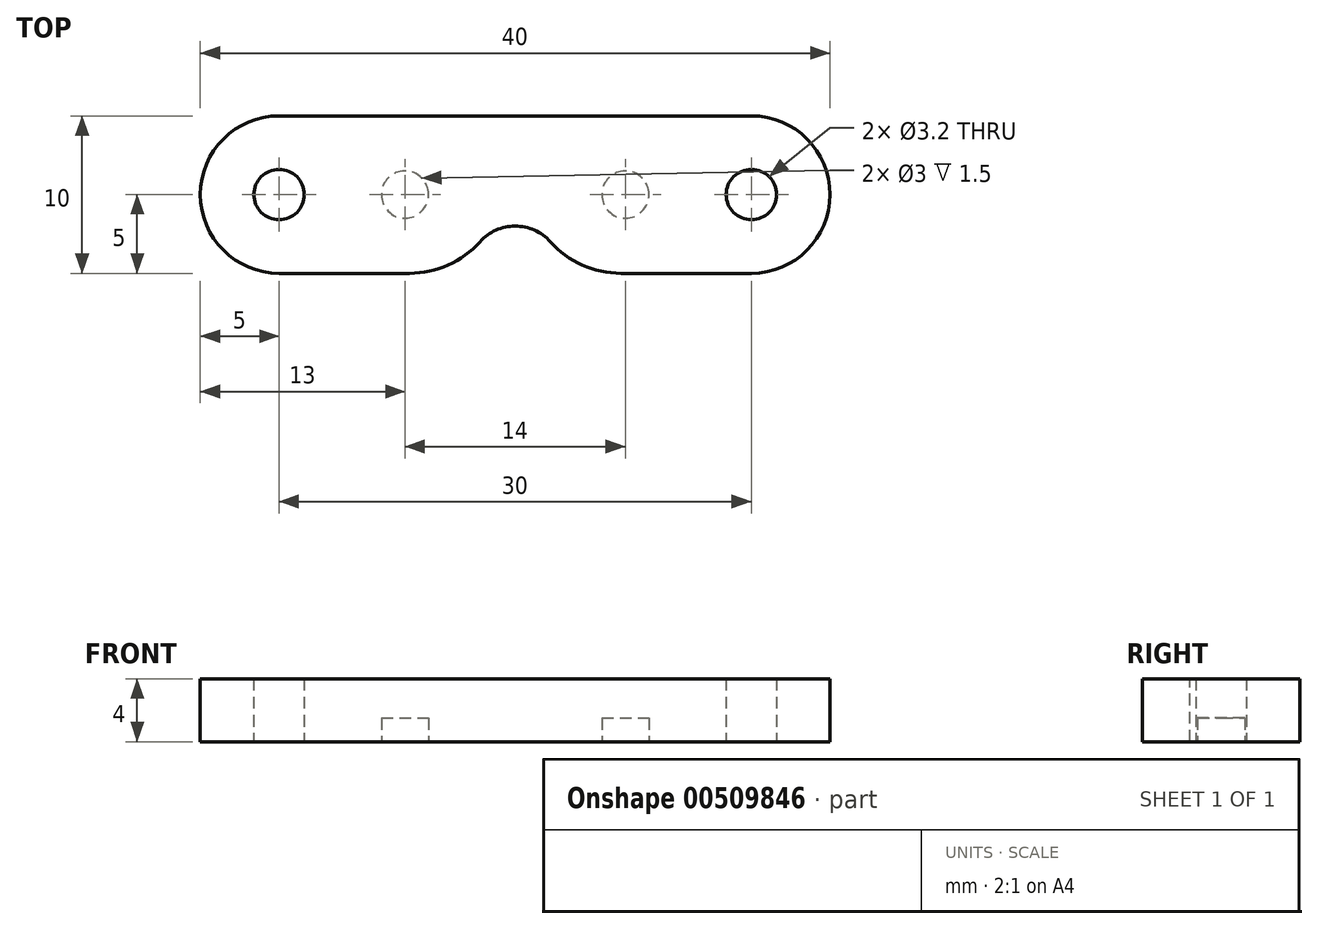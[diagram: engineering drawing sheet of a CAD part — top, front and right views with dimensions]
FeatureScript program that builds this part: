
annotation { "Feature Type Name" : "Feature", "Feature Type Description" : "" }
export const myFeature = defineFeature(function(context is Context, id is Id, definition is map)
    precondition{}
    {
        {
            var Q0;
            Q0=qCreatedBy(makeId("Top.planeOp"),FACE);
            var sketch = newSketch(context, id + "F0", { "sketchPlane" : qUnion([Q0])});
            skLineSegment(sketch, "E0.bottom", {"start": v(20, 5) * mm, "end": v(-20, 5) * mm});
            skLineSegment(sketch, "E0.top", {"start": v(20, -5) * mm, "end": v(-20, -5) * mm});
            skLineSegment(sketch, "E0.left", {"start": v(20, 5) * mm, "end": v(20, -5) * mm});
            skLineSegment(sketch, "E0.right", {"start": v(-20, 5) * mm, "end": v(-20, -5) * mm});
            skPoint(sketch, "E0.middle", {"position": v(0, 0) * mm});
            skCircle(sketch, "E1", {"center": v(-15, 0) * mm, "radius": 1.6 * mm});
            skCircle(sketch, "E2", {"center": v(15, 0) * mm, "radius": 1.6 * mm});
            skSolve(sketch);
        }
        {
            var Q0;
            Q0 = qSketchRegion(id + "F0", true);
            extrude(context, id + "F1", {"entities" : qUnion([Q0]), "depth" : 4 * mm});
        }
        {
            var Q0;
            Q0=makeQuery(id+"F1.opExtrude","CAP_FACE",FACE,{"disambiguationData":[OSD([sQuery(id+"F0.wireOp",EDGE,"E0.bottom"),sQuery(id+"F0.wireOp",EDGE,"E0.top"),sQuery(id+"F0.wireOp",EDGE,"E0.left"),sQuery(id+"F0.wireOp",EDGE,"E0.right"),sQuery(id+"F0.wireOp",EDGE,"E1"),sQuery(id+"F0.wireOp",EDGE,"E2")])],"isStart":true});
            var sketch = newSketch(context, id + "F2", { "sketchPlane" : qUnion([Q0])});
            skCircle(sketch, "E3", {"center": v(-7, 0) * mm, "radius": 1.5 * mm});
            skCircle(sketch, "E4", {"center": v(7, 0) * mm, "radius": 1.5 * mm});
            skSolve(sketch);
        }
        {
            var Q0;
            Q0 = qSketchRegion(id + "F2", true);
            extrude(context, id + "F3", {"entities" : qUnion([Q0]), "operationType" : NewBodyOperationType.REMOVE, "oppositeDirection" : true, "depth" : 1.5 * mm});
        }
        {
            var Q0;
            Q0=makeQuery(id+"F1.opExtrude","SWEPT_EDGE",EDGE,{"disambiguationData":[OSD([sQuery(id+"F0.wireOp",EDGE,"E0.top"),sQuery(id+"F0.wireOp",EDGE,"E0.right")])]});
            var Q1;
            Q1=makeQuery(id+"F1.opExtrude","SWEPT_EDGE",EDGE,{"disambiguationData":[OSD([sQuery(id+"F0.wireOp",EDGE,"E0.bottom"),sQuery(id+"F0.wireOp",EDGE,"E0.right")])]});
            var Q2;
            Q2=makeQuery(id+"F1.opExtrude","SWEPT_EDGE",EDGE,{"disambiguationData":[OSD([sQuery(id+"F0.wireOp",EDGE,"E0.bottom"),sQuery(id+"F0.wireOp",EDGE,"E0.left")])]});
            var Q3;
            Q3=makeQuery(id+"F1.opExtrude","SWEPT_EDGE",EDGE,{"disambiguationData":[OSD([sQuery(id+"F0.wireOp",EDGE,"E0.top"),sQuery(id+"F0.wireOp",EDGE,"E0.left")])]});
            fillet(context, id + "F4", {"entities" : qUnion([Q0, Q1, Q2, Q3]), "radius" : 5 * mm, "tangentPropagation" : true, "allowEdgeOverflow" : false});
        }
        {
            var Q0;
            Q0=makeQuery(id+"F1.opExtrude","CAP_FACE",FACE,{"disambiguationData":[OSD([sQuery(id+"F0.wireOp",EDGE,"E0.bottom"),sQuery(id+"F0.wireOp",EDGE,"E0.top"),sQuery(id+"F0.wireOp",EDGE,"E0.left"),sQuery(id+"F0.wireOp",EDGE,"E0.right"),sQuery(id+"F0.wireOp",EDGE,"E1"),sQuery(id+"F0.wireOp",EDGE,"E2")])],"isStart":false});
            var sketch = newSketch(context, id + "F5", { "sketchPlane" : qUnion([Q0])});
            skCircle(sketch, "E5", {"center": v(0, -5) * mm, "radius": 3 * mm});
            skSolve(sketch);
        }
        {
            var Q0;
            Q0 = qSketchRegion(id + "F5", true);
            extrude(context, id + "F6", {"entities" : qUnion([Q0]), "operationType" : NewBodyOperationType.REMOVE, "oppositeDirection" : true, "depth" : 25 * mm});
        }
        {
            var Q0;
            Q0=makeQuery(id+"F6.boolean.opBoolean","INTERSECT",EDGE,{"disambiguationData":[OD(1.0)],"derivedFrom":[makeQuery(id+"F1.opExtrude","SWEPT_FACE",FACE,{"disambiguationData":[OSD([sQuery(id+"F0.wireOp",EDGE,"E0.top")])]}),makeQuery(id+"F6.opExtrude","SWEPT_FACE",FACE,{"disambiguationData":[OSD([sQuery(id+"F5.wireOp",EDGE,"E5")])]})]});
            var Q1;
            Q1=makeQuery(id+"F6.boolean.opBoolean","INTERSECT",EDGE,{"disambiguationData":[OD(0.0)],"derivedFrom":[makeQuery(id+"F1.opExtrude","SWEPT_FACE",FACE,{"disambiguationData":[OSD([sQuery(id+"F0.wireOp",EDGE,"E0.top")])]}),makeQuery(id+"F6.opExtrude","SWEPT_FACE",FACE,{"disambiguationData":[OSD([sQuery(id+"F5.wireOp",EDGE,"E5")])]})]});
            fillet(context, id + "F7", {"entities" : qUnion([Q0, Q1]), "radius" : 6 * mm, "tangentPropagation" : true, "allowEdgeOverflow" : false});
        }
    });
